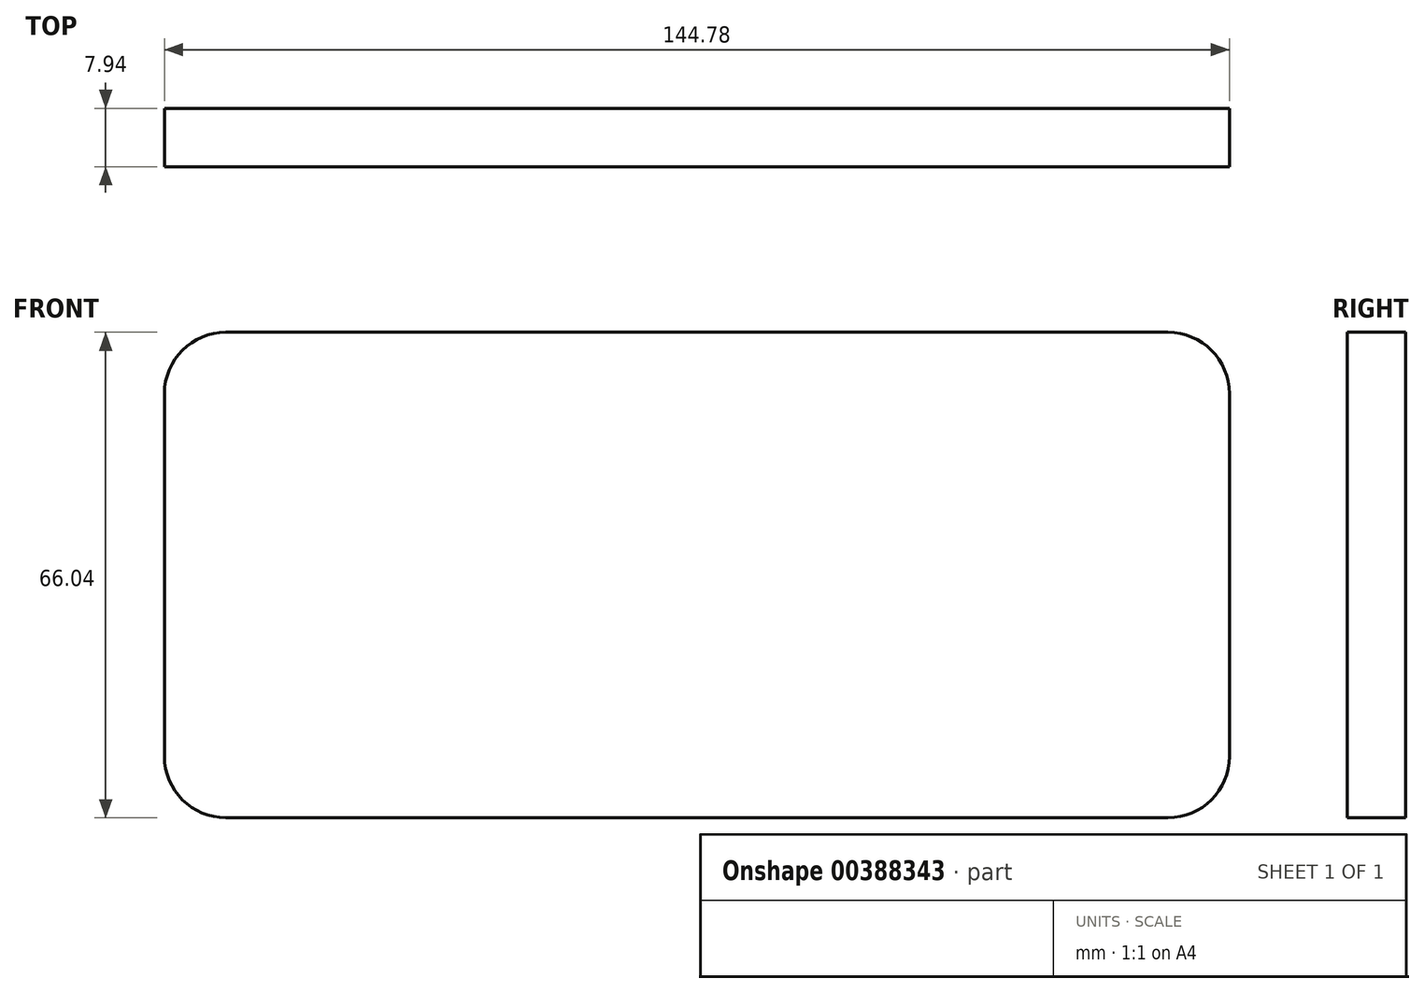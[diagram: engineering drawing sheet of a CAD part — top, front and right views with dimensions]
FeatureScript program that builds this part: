
annotation { "Feature Type Name" : "Feature", "Feature Type Description" : "" }
export const myFeature = defineFeature(function(context is Context, id is Id, definition is map)
    precondition{}
    {
        {
            var Q0;
            Q0=qCreatedBy(makeId("Front.planeOp"),FACE);
            var sketch = newSketch(context, id + "F0", { "sketchPlane" : qUnion([Q0])});
            skLineSegment(sketch, "E0.bottom", {"start": v(0, 0) * mm, "end": v(144.78, 0) * mm});
            skLineSegment(sketch, "E0.top", {"start": v(0, 66.04) * mm, "end": v(144.78, 66.04) * mm});
            skLineSegment(sketch, "E0.left", {"start": v(0, 0) * mm, "end": v(0, 66.04) * mm});
            skLineSegment(sketch, "E0.right", {"start": v(144.78, 0) * mm, "end": v(144.78, 66.04) * mm});
            skSolve(sketch);
        }
        {
            var Q0;
            Q0 = qSketchRegion(id + "F0", true);
            extrude(context, id + "F1", {"entities" : qUnion([Q0]), "depth" : 7.94 * mm});
        }
        {
            var Q0;
            Q0=makeQuery(id+"F1.opExtrude","SWEPT_EDGE",EDGE,{"disambiguationData":[OSD([sQuery(id+"F0.wireOp",EDGE,"E0.top"),sQuery(id+"F0.wireOp",EDGE,"E0.right")])]});
            var Q1;
            Q1=makeQuery(id+"F1.opExtrude","SWEPT_EDGE",EDGE,{"disambiguationData":[OSD([sQuery(id+"F0.wireOp",EDGE,"E0.bottom"),sQuery(id+"F0.wireOp",EDGE,"E0.right")])]});
            var Q2;
            Q2=makeQuery(id+"F1.opExtrude","SWEPT_EDGE",EDGE,{"disambiguationData":[OSD([sQuery(id+"F0.wireOp",EDGE,"E0.top"),sQuery(id+"F0.wireOp",EDGE,"E0.left")])]});
            var Q3;
            Q3=makeQuery(id+"F1.opExtrude","SWEPT_EDGE",EDGE,{"disambiguationData":[OSD([sQuery(id+"F0.wireOp",EDGE,"E0.bottom"),sQuery(id+"F0.wireOp",EDGE,"E0.left")])]});
            fillet(context, id + "F2", {"entities" : qUnion([Q0, Q1, Q2, Q3]), "radius" : 8.36 * mm, "tangentPropagation" : true, "allowEdgeOverflow" : false});
        }
    });
